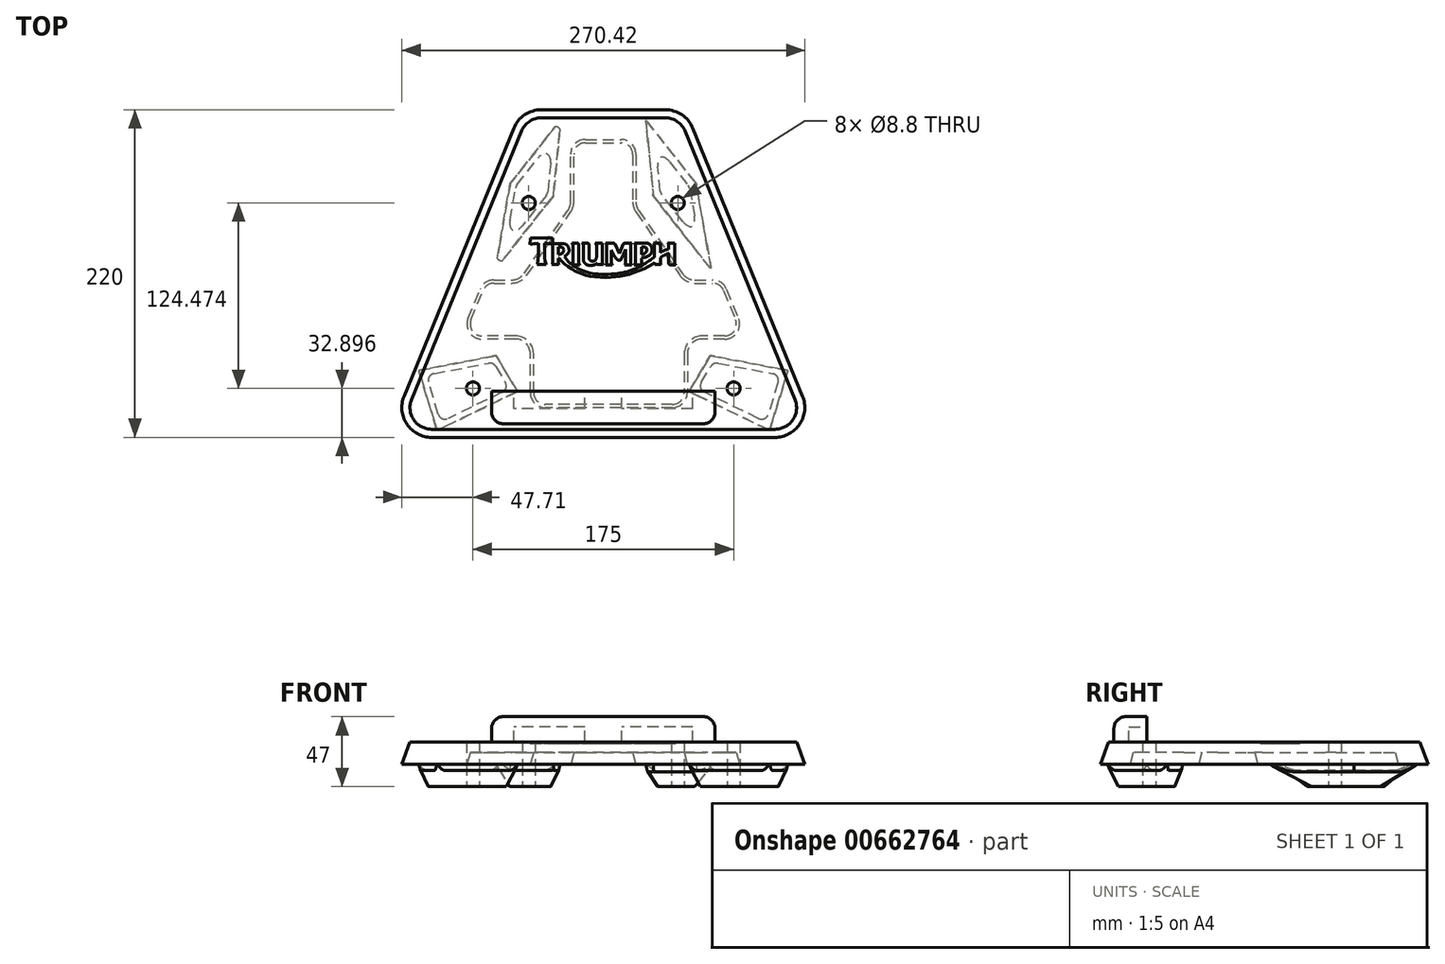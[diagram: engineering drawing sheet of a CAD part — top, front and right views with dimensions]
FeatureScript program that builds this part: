
annotation { "Feature Type Name" : "Feature", "Feature Type Description" : "" }
export const myFeature = defineFeature(function(context is Context, id is Id, definition is map)
    precondition{}
    {
        {
            var Q0;
            Q0=qCreatedBy(makeId("Top.planeOp"),FACE);
            var sketch = newSketch(context, id + "F0", { "sketchPlane" : qUnion([Q0])});
            skPoint(sketch, "E0", {"position": v(-87.5, -62.1) * mm});
            skPoint(sketch, "E1", {"position": v(87.5, -62.1) * mm});
            skPoint(sketch, "E2", {"position": v(50, 62.37) * mm});
            skPoint(sketch, "E3", {"position": v(-50, 62.37) * mm});
            skCircle(sketch, "E4", {"center": v(-50, 62.37) * mm, "radius": 4 * mm});
            skCircle(sketch, "E5", {"center": v(50, 62.37) * mm, "radius": 4 * mm});
            skCircle(sketch, "E6", {"center": v(87.5, -62.1) * mm, "radius": 4 * mm});
            skCircle(sketch, "E7", {"center": v(-87.5, -62.1) * mm, "radius": 4 * mm});
            skSolve(sketch);
        }
        {
            var Q0;
            Q0=qCreatedBy(makeId("Top.planeOp"),FACE);
            var sketch = newSketch(context, id + "F1", { "sketchPlane" : qUnion([Q0])});
            skLineSegment(sketch, "E8.0", {"start": v(72.5, 17.72) * mm, "end": v(62.5, 75.32) * mm});
            skLineSegment(sketch, "E8.1", {"start": v(62.5, 75.32) * mm, "end": v(28.5, 118.39) * mm});
            skLineSegment(sketch, "E8.2", {"start": v(28.5, 118.39) * mm, "end": v(33.5, 67.12) * mm});
            skLineSegment(sketch, "E9", {"start": v(72.5, 17.72) * mm, "end": v(33.5, 67.12) * mm});
            skLineSegment(sketch, "E10", {"start": v(-62.5, 75.32) * mm, "end": v(-28.5, 118.39) * mm});
            skLineSegment(sketch, "E11", {"start": v(-28.5, 118.39) * mm, "end": v(-33.5, 67.12) * mm});
            skLineSegment(sketch, "E12", {"start": v(-33.5, 67.12) * mm, "end": v(-72.5, 17.72) * mm});
            skLineSegment(sketch, "E13", {"start": v(-72.5, 17.72) * mm, "end": v(-62.5, 75.32) * mm});
            skPoint(sketch, "E14", {"position": v(-71.85, -40.1) * mm});
            skPoint(sketch, "E15", {"position": v(-57.57, -64.2) * mm});
            skPoint(sketch, "E16", {"position": v(-123.9, -50.1) * mm});
            skPoint(sketch, "E17", {"position": v(-111.61, -90.27) * mm});
            skPoint(sketch, "E18", {"position": v(71.85, -40.1) * mm});
            skPoint(sketch, "E19", {"position": v(57.57, -64.2) * mm});
            skPoint(sketch, "E20", {"position": v(123.9, -50.1) * mm});
            skPoint(sketch, "E21", {"position": v(111.61, -90.27) * mm});
            skLineSegment(sketch, "E22", {"start": v(-123.9, -50.1) * mm, "end": v(-71.85, -40.1) * mm});
            skLineSegment(sketch, "E23", {"start": v(-57.57, -64.2) * mm, "end": v(-71.85, -40.1) * mm});
            skLineSegment(sketch, "E24", {"start": v(-57.57, -64.2) * mm, "end": v(-111.61, -90.27) * mm});
            skLineSegment(sketch, "E25", {"start": v(-111.61, -90.27) * mm, "end": v(-123.9, -50.1) * mm});
            skLineSegment(sketch, "E26", {"start": v(57.57, -64.2) * mm, "end": v(71.85, -40.1) * mm});
            skLineSegment(sketch, "E27", {"start": v(71.85, -40.1) * mm, "end": v(123.9, -50.1) * mm});
            skLineSegment(sketch, "E28", {"start": v(123.9, -50.1) * mm, "end": v(111.61, -90.27) * mm});
            skLineSegment(sketch, "E29", {"start": v(111.61, -90.27) * mm, "end": v(57.57, -64.2) * mm});
            skSolve(sketch);
        }
        {
            var Q0;
            Q0=makeQuery(id+"F1.imprint","IMPRINT",FACE,{"disambiguationData":[TD([[makeQuery(id+"F1.imprint","IMPRINT",EDGE,{"derivedFrom":sQuery(id+"F1.wireOp",EDGE,"E22")}),-1.0]])]});
            var Q1;
            Q1=makeQuery(id+"F1.imprint","IMPRINT",FACE,{"disambiguationData":[TD([[makeQuery(id+"F1.imprint","IMPRINT",EDGE,{"derivedFrom":sQuery(id+"F1.wireOp",EDGE,"E10")}),-1.0]])]});
            var Q2;
            Q2=makeQuery(id+"F1.imprint","IMPRINT",FACE,{"disambiguationData":[TD([[makeQuery(id+"F1.imprint","IMPRINT",EDGE,{"derivedFrom":sQuery(id+"F1.wireOp",EDGE,"E8.0")}),1.0]])]});
            var Q3;
            Q3=makeQuery(id+"F1.imprint","IMPRINT",FACE,{"disambiguationData":[TD([[makeQuery(id+"F1.imprint","IMPRINT",EDGE,{"derivedFrom":sQuery(id+"F1.wireOp",EDGE,"E26")}),-1.0]])]});
            extrude(context, id + "F2", {"entities" : qUnion([Q0, Q1, Q2, Q3]), "depth" : 15 * mm, "offsetDistance" : 25 * mm});
        }
        {
            var Q0;
            Q0=makeQuery(id+"F2.opExtrude","CAP_FACE",FACE,{"disambiguationData":[OSD([sQuery(id+"F1.wireOp",EDGE,"E10"),sQuery(id+"F1.wireOp",EDGE,"E11"),sQuery(id+"F1.wireOp",EDGE,"E12"),sQuery(id+"F1.wireOp",EDGE,"E13")])],"isStart":false});
            var sketch = newSketch(context, id + "F3", { "sketchPlane" : qUnion([Q0])});
            skLineSegment(sketch, "E30.bottom", {"start": v(-41.57, 125) * mm, "end": v(41.57, 125) * mm});
            skLineSegment(sketch, "E30.top", {"start": v(-115.2, -95) * mm, "end": v(115.2, -95) * mm});
            skLineSegment(sketch, "E30.left", {"start": v(-60.08, 112.57) * mm, "end": v(-133.72, -67.43) * mm});
            skLineSegment(sketch, "E30.right", {"start": v(60.08, 112.57) * mm, "end": v(133.72, -67.43) * mm});
            skPoint(sketch, "E31.visualSharp", {"position": v(-145, -95) * mm});
            skArc(sketch, "E31.filletArc", {"start": v(-133.72, -67.43) * mm, "mid": v(-131.81, -86.15) * mm, "end": v(-115.2, -95) * mm});
            skPoint(sketch, "E32.visualSharp", {"position": v(145, -95) * mm});
            skArc(sketch, "E32.filletArc", {"start": v(115.2, -95) * mm, "mid": v(131.81, -86.15) * mm, "end": v(133.72, -67.43) * mm});
            skPoint(sketch, "E33.visualSharp", {"position": v(55, 125) * mm});
            skArc(sketch, "E33.filletArc", {"start": v(60.08, 112.57) * mm, "mid": v(52.72, 121.6) * mm, "end": v(41.57, 125) * mm});
            skPoint(sketch, "E34.visualSharp", {"position": v(-55, 125) * mm});
            skArc(sketch, "E34.filletArc", {"start": v(-41.57, 125) * mm, "mid": v(-52.72, 121.6) * mm, "end": v(-60.08, 112.57) * mm});
            skSolve(sketch);
        }
        {
            var Q0;
            Q0=makeQuery(id+"F3.imprint","IMPRINT",FACE,{"disambiguationData":[TD([[makeQuery(id+"F3.imprint","IMPRINT",EDGE,{"derivedFrom":sQuery(id+"F3.wireOp",EDGE,"E30.bottom")}),-1.0]])]});
            var Q1;
            Q1=makeQuery(id+"F3.imprint","IMPRINT",FACE,{"disambiguationData":[TD([[makeQuery(id+"F3.imprint","IMPRINT",EDGE,{"derivedFrom":makeQuery(id+"F2.opExtrude","CAP_EDGE",EDGE,{"disambiguationData":[OSD([sQuery(id+"F1.wireOp",EDGE,"E10")])],"isStart":false})}),-1.0]])]});
            extrude(context, id + "F4", {"entities" : qUnion([Q0, Q1]), "depth" : 15 * mm, "offsetDistance" : 25 * mm});
        }
        {
            var Q0;
            Q0=makeQuery(id+"F4.opExtrude","CAP_FACE",FACE,{"disambiguationData":[OSD([sQuery(id+"F3.wireOp",EDGE,"E30.bottom"),sQuery(id+"F3.wireOp",EDGE,"E30.top"),sQuery(id+"F3.wireOp",EDGE,"E30.left"),sQuery(id+"F3.wireOp",EDGE,"E30.right"),sQuery(id+"F3.wireOp",EDGE,"E31.filletArc"),sQuery(id+"F3.wireOp",EDGE,"E32.filletArc"),sQuery(id+"F3.wireOp",EDGE,"E33.filletArc"),sQuery(id+"F3.wireOp",EDGE,"E34.filletArc")])],"isStart":false});
            chamfer(context, id + "F5", {"entities" : qUnion([Q0]), "chamferType" : ChamferType.OFFSET_ANGLE, "width" : 15 * mm, "oppositeDirection" : false, "angle" : 20 * degree, "tangentPropagation" : true});
        }
        {
            var Q0;
            Q0=sQuery(id+"F0.wireOp",VERTEX,"E7.center");
            var Q1;
            Q1=sQuery(id+"F0.wireOp",VERTEX,"E4.center");
            var Q2;
            Q2=sQuery(id+"F0.wireOp",VERTEX,"E2");
            var Q3;
            Q3=sQuery(id+"F0.wireOp",VERTEX,"E1");
            var Q4;
            Q4=makeQuery(id+"F2.opExtrude","SWEPT_BODY",BODY,{"disambiguationData":[OSD([sQuery(id+"F1.wireOp",EDGE,"E22"),sQuery(id+"F1.wireOp",EDGE,"E23"),sQuery(id+"F1.wireOp",EDGE,"E24"),sQuery(id+"F1.wireOp",EDGE,"E25")])]});
            var Q5;
            Q5=makeQuery(id+"F4.opExtrude","SWEPT_BODY",BODY,{"disambiguationData":[OSD([sQuery(id+"F3.wireOp",EDGE,"E30.bottom"),sQuery(id+"F3.wireOp",EDGE,"E30.top"),sQuery(id+"F3.wireOp",EDGE,"E30.left"),sQuery(id+"F3.wireOp",EDGE,"E30.right"),sQuery(id+"F3.wireOp",EDGE,"E31.filletArc"),sQuery(id+"F3.wireOp",EDGE,"E32.filletArc"),sQuery(id+"F3.wireOp",EDGE,"E33.filletArc"),sQuery(id+"F3.wireOp",EDGE,"E34.filletArc")])]});
            var Q6;
            Q6=makeQuery(id+"F2.opExtrude","SWEPT_BODY",BODY,{"disambiguationData":[OSD([sQuery(id+"F1.wireOp",EDGE,"E10"),sQuery(id+"F1.wireOp",EDGE,"E11"),sQuery(id+"F1.wireOp",EDGE,"E12"),sQuery(id+"F1.wireOp",EDGE,"E13")])]});
            var Q7;
            Q7=makeQuery(id+"F2.opExtrude","SWEPT_BODY",BODY,{"disambiguationData":[OSD([sQuery(id+"F1.wireOp",EDGE,"E8.0"),sQuery(id+"F1.wireOp",EDGE,"E8.1"),sQuery(id+"F1.wireOp",EDGE,"E8.2"),sQuery(id+"F1.wireOp",EDGE,"E9")])]});
            var Q8;
            Q8=makeQuery(id+"F2.opExtrude","SWEPT_BODY",BODY,{"disambiguationData":[OSD([sQuery(id+"F1.wireOp",EDGE,"E26"),sQuery(id+"F1.wireOp",EDGE,"E27"),sQuery(id+"F1.wireOp",EDGE,"E28"),sQuery(id+"F1.wireOp",EDGE,"E29")])]});
            hole(context, id + "F6", {"style" : HoleStyle.SIMPLE, "endStyle" : HoleEndStyle.THROUGH, "oppositeDirection" : true, "standardTappedOrClearance" : lookupTablePath({ "standard" : "ISO", "fit" : "Normal", "size" : "M8", "type" : "Clearance" }), "standardBlindInLast" : lookupTablePath({ "fit" : "Standard", "standard" : "ISO", "size" : "M8", "type" : "Clearance" }), "holeDiameter" : 8.8 * mm, "majorDiameter" : 5 * mm, "isTappedThrough" : true, "tappedDepth" : 12 * mm, "tapClearance" : 3, "locations" : qUnion([Q0, Q1, Q2, Q3]), "scope" : qUnion([Q4, Q5, Q6, Q7, Q8])});
        }
        {
            var Q0;
            Q0=makeQuery(id+"F4.opExtrude","CAP_FACE",FACE,{"disambiguationData":[OSD([sQuery(id+"F3.wireOp",EDGE,"E30.bottom"),sQuery(id+"F3.wireOp",EDGE,"E30.top"),sQuery(id+"F3.wireOp",EDGE,"E30.left"),sQuery(id+"F3.wireOp",EDGE,"E30.right"),sQuery(id+"F3.wireOp",EDGE,"E31.filletArc"),sQuery(id+"F3.wireOp",EDGE,"E32.filletArc"),sQuery(id+"F3.wireOp",EDGE,"E33.filletArc"),sQuery(id+"F3.wireOp",EDGE,"E34.filletArc")])],"isStart":true});
            var sketch = newSketch(context, id + "F7", { "sketchPlane" : qUnion([Q0])});
            skLineSegment(sketch, "E35.0", {"start": v(-115.2, 75) * mm, "end": v(-115.2, 75) * mm});
            skLineSegment(sketch, "E35.1", {"start": v(-82.69, -4.5) * mm, "end": v(-90.76, 15.23) * mm});
            skLineSegment(sketch, "E35.2", {"start": v(-38.95, 75) * mm, "end": v(46.4, 75) * mm});
            skLineSegment(sketch, "E35.3", {"start": v(-41.57, -105) * mm, "end": v(-41.57, -105) * mm});
            skLineSegment(sketch, "E35.4", {"start": v(115.2, 75) * mm, "end": v(115.2, 75) * mm});
            skLineSegment(sketch, "E35.5", {"start": v(82.69, -4.5) * mm, "end": v(90.76, 15.23) * mm});
            skLineSegment(sketch, "E35.6", {"start": v(41.57, -105) * mm, "end": v(41.57, -105) * mm});
            skLineSegment(sketch, "E35.7", {"start": v(-11.93, -105) * mm, "end": v(11.93, -105) * mm});
            skLineSegment(sketch, "E36", {"start": v(-81.5, 29.02) * mm, "end": v(-58.95, 29.02) * mm});
            skLineSegment(sketch, "E37", {"start": v(-48.95, 65) * mm, "end": v(-48.95, 39.02) * mm});
            skLineSegment(sketch, "E38", {"start": v(81.5, 29.02) * mm, "end": v(66.4, 29.02) * mm});
            skLineSegment(sketch, "E39", {"start": v(56.4, 65) * mm, "end": v(56.4, 39.02) * mm});
            skPoint(sketch, "E40.newPointA", {"position": v(-88.95, 29.02) * mm});
            skArc(sketch, "E40.filletArc", {"start": v(-81.5, 29.02) * mm, "mid": v(-89.8, 24.59) * mm, "end": v(-90.76, 15.23) * mm});
            skPoint(sketch, "E41.visualSharp", {"position": v(-48.95, 29.02) * mm});
            skArc(sketch, "E41.filletArc", {"start": v(-58.95, 29.02) * mm, "mid": v(-51.88, 31.94) * mm, "end": v(-48.95, 39.02) * mm});
            skPoint(sketch, "E42.newPointA", {"position": v(-48.95, 75) * mm});
            skArc(sketch, "E42.filletArc", {"start": v(-38.95, 75) * mm, "mid": v(-46.02, 72.07) * mm, "end": v(-48.95, 65) * mm});
            skPoint(sketch, "E43.newPointB", {"position": v(56.4, 75) * mm});
            skArc(sketch, "E43.filletArc", {"start": v(56.4, 65) * mm, "mid": v(53.47, 72.07) * mm, "end": v(46.4, 75) * mm});
            skPoint(sketch, "E44.visualSharp", {"position": v(56.4, 29.02) * mm});
            skArc(sketch, "E44.filletArc", {"start": v(56.4, 39.02) * mm, "mid": v(59.33, 31.94) * mm, "end": v(66.4, 29.02) * mm});
            skPoint(sketch, "E45.newPointA", {"position": v(96.4, 29.02) * mm});
            skArc(sketch, "E45.filletArc", {"start": v(90.76, 15.23) * mm, "mid": v(89.8, 24.59) * mm, "end": v(81.5, 29.02) * mm});
            skLineSegment(sketch, "E46", {"start": v(-73.43, -10.71) * mm, "end": v(-61.38, -10.71) * mm});
            skLineSegment(sketch, "E47", {"start": v(73.43, -10.71) * mm, "end": v(61.38, -10.71) * mm});
            skLineSegment(sketch, "E48", {"start": v(-21.93, -95) * mm, "end": v(-21.93, -63.13) * mm});
            skLineSegment(sketch, "E49", {"start": v(-23.71, -57.43) * mm, "end": v(-53.16, -15) * mm});
            skLineSegment(sketch, "E50", {"start": v(21.93, -95) * mm, "end": v(21.93, -63.13) * mm});
            skLineSegment(sketch, "E51", {"start": v(23.71, -57.43) * mm, "end": v(53.16, -15) * mm});
            skPoint(sketch, "E52.newPointA", {"position": v(-80.15, -10.71) * mm});
            skArc(sketch, "E52.filletArc", {"start": v(-82.69, -4.5) * mm, "mid": v(-79, -9.01) * mm, "end": v(-73.43, -10.71) * mm});
            skPoint(sketch, "E53.visualSharp", {"position": v(-56.15, -10.71) * mm});
            skArc(sketch, "E53.filletArc", {"start": v(-53.16, -15) * mm, "mid": v(-56.74, -11.85) * mm, "end": v(-61.38, -10.71) * mm});
            skPoint(sketch, "E54.visualSharp", {"position": v(-21.93, -60) * mm});
            skArc(sketch, "E54.filletArc", {"start": v(-21.93, -63.13) * mm, "mid": v(-22.38, -60.14) * mm, "end": v(-23.71, -57.43) * mm});
            skPoint(sketch, "E55.newPointA", {"position": v(-21.93, -105) * mm});
            skArc(sketch, "E55.filletArc", {"start": v(-21.93, -95) * mm, "mid": v(-19, -102.07) * mm, "end": v(-11.93, -105) * mm});
            skPoint(sketch, "E56.newPointA", {"position": v(21.93, -105) * mm});
            skArc(sketch, "E56.filletArc", {"start": v(11.93, -105) * mm, "mid": v(19, -102.07) * mm, "end": v(21.93, -95) * mm});
            skPoint(sketch, "E57.visualSharp", {"position": v(21.93, -60) * mm});
            skArc(sketch, "E57.filletArc", {"start": v(23.71, -57.43) * mm, "mid": v(22.38, -60.14) * mm, "end": v(21.93, -63.13) * mm});
            skPoint(sketch, "E58.visualSharp", {"position": v(56.15, -10.71) * mm});
            skArc(sketch, "E58.filletArc", {"start": v(61.38, -10.71) * mm, "mid": v(56.74, -11.85) * mm, "end": v(53.16, -15) * mm});
            skPoint(sketch, "E59.newPointA", {"position": v(80.15, -10.71) * mm});
            skArc(sketch, "E59.filletArc", {"start": v(73.43, -10.71) * mm, "mid": v(79, -9.01) * mm, "end": v(82.69, -4.5) * mm});
            skSolve(sketch);
        }
        {
            var Q0;
            Q0=makeQuery(id+"F7.imprint","IMPRINT",FACE,{"disambiguationData":[TD([[makeQuery(id+"F7.imprint","IMPRINT",EDGE,{"derivedFrom":sQuery(id+"F7.wireOp",EDGE,"E35.1")}),-1.0]])]});
            extrude(context, id + "F8", {"entities" : qUnion([Q0]), "operationType" : NewBodyOperationType.REMOVE, "oppositeDirection" : true, "depth" : 8 * mm, "offsetDistance" : 25 * mm, "hasDraft" : true, "draftAngle" : 15 * degree, "draftPullDirection" : true});
        }
        {
            var Q0;
            Q0=makeQuery(id+"F2.opExtrude","CAP_EDGE",EDGE,{"disambiguationData":[OSD([sQuery(id+"F1.wireOp",EDGE,"E27")])],"isStart":true});
            var Q1;
            Q1=makeQuery(id+"F2.opExtrude","CAP_EDGE",EDGE,{"disambiguationData":[OSD([sQuery(id+"F1.wireOp",EDGE,"E28")])],"isStart":true});
            var Q2;
            Q2=makeQuery(id+"F2.opExtrude","CAP_EDGE",EDGE,{"disambiguationData":[OSD([sQuery(id+"F1.wireOp",EDGE,"E29")])],"isStart":true});
            var Q3;
            Q3=makeQuery(id+"F2.opExtrude","CAP_EDGE",EDGE,{"disambiguationData":[OSD([sQuery(id+"F1.wireOp",EDGE,"E26")])],"isStart":true});
            var Q4;
            Q4=makeQuery(id+"F2.opExtrude","CAP_EDGE",EDGE,{"disambiguationData":[OSD([sQuery(id+"F1.wireOp",EDGE,"E25")])],"isStart":true});
            var Q5;
            Q5=makeQuery(id+"F2.opExtrude","CAP_EDGE",EDGE,{"disambiguationData":[OSD([sQuery(id+"F1.wireOp",EDGE,"E24")])],"isStart":true});
            var Q6;
            Q6=makeQuery(id+"F2.opExtrude","CAP_EDGE",EDGE,{"disambiguationData":[OSD([sQuery(id+"F1.wireOp",EDGE,"E23")])],"isStart":true});
            var Q7;
            Q7=makeQuery(id+"F2.opExtrude","CAP_EDGE",EDGE,{"disambiguationData":[OSD([sQuery(id+"F1.wireOp",EDGE,"E22")])],"isStart":true});
            var Q8;
            Q8=makeQuery(id+"F2.opExtrude","CAP_EDGE",EDGE,{"disambiguationData":[OSD([sQuery(id+"F1.wireOp",EDGE,"E11")])],"isStart":true});
            var Q9;
            Q9=makeQuery(id+"F2.opExtrude","CAP_EDGE",EDGE,{"disambiguationData":[OSD([sQuery(id+"F1.wireOp",EDGE,"E10")])],"isStart":true});
            var Q10;
            Q10=makeQuery(id+"F2.opExtrude","CAP_EDGE",EDGE,{"disambiguationData":[OSD([sQuery(id+"F1.wireOp",EDGE,"E13")])],"isStart":true});
            var Q11;
            Q11=makeQuery(id+"F2.opExtrude","CAP_EDGE",EDGE,{"disambiguationData":[OSD([sQuery(id+"F1.wireOp",EDGE,"E12")])],"isStart":true});
            chamfer(context, id + "F9", {"entities" : qUnion([Q0, Q1, Q2, Q3, Q4, Q5, Q6, Q7, Q8, Q9, Q10, Q11]), "chamferType" : ChamferType.TWO_OFFSETS, "width1" : 4 * mm, "oppositeDirection" : false, "width2" : 11 * mm, "tangentPropagation" : true});
        }
        {
            var Q0;
            Q0=makeQuery(id+"F2.opExtrude","CAP_EDGE",EDGE,{"disambiguationData":[OSD([sQuery(id+"F1.wireOp",EDGE,"E8.1")])],"isStart":true});
            var Q1;
            Q1=makeQuery(id+"F2.opExtrude","CAP_EDGE",EDGE,{"disambiguationData":[OSD([sQuery(id+"F1.wireOp",EDGE,"E8.2")])],"isStart":true});
            var Q2;
            Q2=makeQuery(id+"F2.opExtrude","CAP_EDGE",EDGE,{"disambiguationData":[OSD([sQuery(id+"F1.wireOp",EDGE,"E9")])],"isStart":true});
            var Q3;
            Q3=makeQuery(id+"F2.opExtrude","CAP_EDGE",EDGE,{"disambiguationData":[OSD([sQuery(id+"F1.wireOp",EDGE,"E8.0")])],"isStart":true});
            chamfer(context, id + "F10", {"entities" : qUnion([Q0, Q1, Q2, Q3]), "chamferType" : ChamferType.TWO_OFFSETS, "width1" : 10 * mm, "oppositeDirection" : false, "width2" : 5 * mm, "tangentPropagation" : true});
        }
        {
            var Q0;
            Q0=makeQuery(id+"F9.opChamfer","BLEND_EDGE",EDGE,{"blendedFrom":[makeQuery(id+"F2.opExtrude","CAP_EDGE",EDGE,{"disambiguationData":[OSD([sQuery(id+"F1.wireOp",EDGE,"E24")])],"isStart":true}),makeQuery(id+"F2.opExtrude","CAP_EDGE",EDGE,{"disambiguationData":[OSD([sQuery(id+"F1.wireOp",EDGE,"E25")])],"isStart":true})],"blendedInto":[]});
            var Q1;
            Q1=makeQuery(id+"F9.opChamfer","BLEND_EDGE",EDGE,{"blendedFrom":[makeQuery(id+"F2.opExtrude","CAP_EDGE",EDGE,{"disambiguationData":[OSD([sQuery(id+"F1.wireOp",EDGE,"E22")])],"isStart":true}),makeQuery(id+"F2.opExtrude","CAP_EDGE",EDGE,{"disambiguationData":[OSD([sQuery(id+"F1.wireOp",EDGE,"E25")])],"isStart":true})],"blendedInto":[]});
            var Q2;
            Q2=makeQuery(id+"F9.opChamfer","BLEND_EDGE",EDGE,{"blendedFrom":[makeQuery(id+"F2.opExtrude","CAP_EDGE",EDGE,{"disambiguationData":[OSD([sQuery(id+"F1.wireOp",EDGE,"E22")])],"isStart":true}),makeQuery(id+"F2.opExtrude","CAP_EDGE",EDGE,{"disambiguationData":[OSD([sQuery(id+"F1.wireOp",EDGE,"E23")])],"isStart":true})],"blendedInto":[]});
            var Q3;
            Q3=makeQuery(id+"F9.opChamfer","BLEND_EDGE",EDGE,{"blendedFrom":[makeQuery(id+"F2.opExtrude","CAP_EDGE",EDGE,{"disambiguationData":[OSD([sQuery(id+"F1.wireOp",EDGE,"E23")])],"isStart":true}),makeQuery(id+"F2.opExtrude","CAP_EDGE",EDGE,{"disambiguationData":[OSD([sQuery(id+"F1.wireOp",EDGE,"E24")])],"isStart":true})],"blendedInto":[]});
            var Q4;
            Q4=makeQuery(id+"F9.opChamfer","BLEND_EDGE",EDGE,{"blendedFrom":[makeQuery(id+"F2.opExtrude","CAP_EDGE",EDGE,{"disambiguationData":[OSD([sQuery(id+"F1.wireOp",EDGE,"E26")])],"isStart":true}),makeQuery(id+"F2.opExtrude","CAP_EDGE",EDGE,{"disambiguationData":[OSD([sQuery(id+"F1.wireOp",EDGE,"E29")])],"isStart":true})],"blendedInto":[]});
            var Q5;
            Q5=makeQuery(id+"F9.opChamfer","BLEND_EDGE",EDGE,{"blendedFrom":[makeQuery(id+"F2.opExtrude","CAP_EDGE",EDGE,{"disambiguationData":[OSD([sQuery(id+"F1.wireOp",EDGE,"E28")])],"isStart":true}),makeQuery(id+"F2.opExtrude","CAP_EDGE",EDGE,{"disambiguationData":[OSD([sQuery(id+"F1.wireOp",EDGE,"E29")])],"isStart":true})],"blendedInto":[]});
            var Q6;
            Q6=makeQuery(id+"F9.opChamfer","BLEND_EDGE",EDGE,{"blendedFrom":[makeQuery(id+"F2.opExtrude","CAP_EDGE",EDGE,{"disambiguationData":[OSD([sQuery(id+"F1.wireOp",EDGE,"E27")])],"isStart":true}),makeQuery(id+"F2.opExtrude","CAP_EDGE",EDGE,{"disambiguationData":[OSD([sQuery(id+"F1.wireOp",EDGE,"E28")])],"isStart":true})],"blendedInto":[]});
            var Q7;
            Q7=makeQuery(id+"F9.opChamfer","BLEND_EDGE",EDGE,{"blendedFrom":[makeQuery(id+"F2.opExtrude","CAP_EDGE",EDGE,{"disambiguationData":[OSD([sQuery(id+"F1.wireOp",EDGE,"E26")])],"isStart":true}),makeQuery(id+"F2.opExtrude","CAP_EDGE",EDGE,{"disambiguationData":[OSD([sQuery(id+"F1.wireOp",EDGE,"E27")])],"isStart":true})],"blendedInto":[]});
            var Q8;
            Q8=makeQuery(id+"F10.opChamfer","BLEND_EDGE",EDGE,{"blendedFrom":[makeQuery(id+"F2.opExtrude","CAP_EDGE",EDGE,{"disambiguationData":[OSD([sQuery(id+"F1.wireOp",EDGE,"E8.1")])],"isStart":true}),makeQuery(id+"F2.opExtrude","CAP_EDGE",EDGE,{"disambiguationData":[OSD([sQuery(id+"F1.wireOp",EDGE,"E8.2")])],"isStart":true})],"blendedInto":[]});
            var Q9;
            Q9=makeQuery(id+"F10.opChamfer","BLEND_EDGE",EDGE,{"blendedFrom":[makeQuery(id+"F2.opExtrude","CAP_EDGE",EDGE,{"disambiguationData":[OSD([sQuery(id+"F1.wireOp",EDGE,"E8.2")])],"isStart":true}),makeQuery(id+"F2.opExtrude","CAP_EDGE",EDGE,{"disambiguationData":[OSD([sQuery(id+"F1.wireOp",EDGE,"E9")])],"isStart":true})],"blendedInto":[]});
            var Q10;
            Q10=makeQuery(id+"F10.opChamfer","BLEND_EDGE",EDGE,{"blendedFrom":[makeQuery(id+"F2.opExtrude","CAP_EDGE",EDGE,{"disambiguationData":[OSD([sQuery(id+"F1.wireOp",EDGE,"E8.0")])],"isStart":true}),makeQuery(id+"F2.opExtrude","CAP_EDGE",EDGE,{"disambiguationData":[OSD([sQuery(id+"F1.wireOp",EDGE,"E9")])],"isStart":true})],"blendedInto":[]});
            var Q11;
            Q11=makeQuery(id+"F10.opChamfer","BLEND_EDGE",EDGE,{"blendedFrom":[makeQuery(id+"F2.opExtrude","CAP_EDGE",EDGE,{"disambiguationData":[OSD([sQuery(id+"F1.wireOp",EDGE,"E8.0")])],"isStart":true}),makeQuery(id+"F2.opExtrude","CAP_EDGE",EDGE,{"disambiguationData":[OSD([sQuery(id+"F1.wireOp",EDGE,"E8.1")])],"isStart":true})],"blendedInto":[]});
            var Q12;
            Q12=makeQuery(id+"F9.opChamfer","BLEND_EDGE",EDGE,{"blendedFrom":[makeQuery(id+"F2.opExtrude","CAP_EDGE",EDGE,{"disambiguationData":[OSD([sQuery(id+"F1.wireOp",EDGE,"E11")])],"isStart":true}),makeQuery(id+"F2.opExtrude","CAP_EDGE",EDGE,{"disambiguationData":[OSD([sQuery(id+"F1.wireOp",EDGE,"E12")])],"isStart":true})],"blendedInto":[]});
            var Q13;
            Q13=makeQuery(id+"F9.opChamfer","BLEND_EDGE",EDGE,{"blendedFrom":[makeQuery(id+"F2.opExtrude","CAP_EDGE",EDGE,{"disambiguationData":[OSD([sQuery(id+"F1.wireOp",EDGE,"E10")])],"isStart":true}),makeQuery(id+"F2.opExtrude","CAP_EDGE",EDGE,{"disambiguationData":[OSD([sQuery(id+"F1.wireOp",EDGE,"E11")])],"isStart":true})],"blendedInto":[]});
            var Q14;
            Q14=makeQuery(id+"F9.opChamfer","BLEND_EDGE",EDGE,{"blendedFrom":[makeQuery(id+"F2.opExtrude","CAP_EDGE",EDGE,{"disambiguationData":[OSD([sQuery(id+"F1.wireOp",EDGE,"E10")])],"isStart":true}),makeQuery(id+"F2.opExtrude","CAP_EDGE",EDGE,{"disambiguationData":[OSD([sQuery(id+"F1.wireOp",EDGE,"E13")])],"isStart":true})],"blendedInto":[]});
            var Q15;
            Q15=makeQuery(id+"F9.opChamfer","BLEND_EDGE",EDGE,{"blendedFrom":[makeQuery(id+"F2.opExtrude","CAP_EDGE",EDGE,{"disambiguationData":[OSD([sQuery(id+"F1.wireOp",EDGE,"E12")])],"isStart":true}),makeQuery(id+"F2.opExtrude","CAP_EDGE",EDGE,{"disambiguationData":[OSD([sQuery(id+"F1.wireOp",EDGE,"E13")])],"isStart":true})],"blendedInto":[]});
            fillet(context, id + "F11", {"entities" : qUnion([Q0, Q1, Q2, Q3, Q4, Q5, Q6, Q7, Q8, Q9, Q10, Q11, Q12, Q13, Q14, Q15]), "radius" : 5 * mm, "tangentPropagation" : true, "allowEdgeOverflow" : false});
        }
        {
            var Q0;
            Q0=makeQuery(id+"F4.opExtrude","CAP_FACE",FACE,{"disambiguationData":[OSD([sQuery(id+"F3.wireOp",EDGE,"E30.bottom"),sQuery(id+"F3.wireOp",EDGE,"E30.top"),sQuery(id+"F3.wireOp",EDGE,"E30.left"),sQuery(id+"F3.wireOp",EDGE,"E30.right"),sQuery(id+"F3.wireOp",EDGE,"E31.filletArc"),sQuery(id+"F3.wireOp",EDGE,"E32.filletArc"),sQuery(id+"F3.wireOp",EDGE,"E33.filletArc"),sQuery(id+"F3.wireOp",EDGE,"E34.filletArc")])],"isStart":false});
            var sketch = newSketch(context, id + "F12", { "sketchPlane" : qUnion([Q0])});
            skLineSegment(sketch, "E60", {"start": v(-48.95, 39) * mm, "end": v(-33.85, 39) * mm});
            skLineSegment(sketch, "E61", {"start": v(-33.85, 39) * mm, "end": v(-33.85, 33.8) * mm});
            skLineSegment(sketch, "E62", {"start": v(-33.85, 33.8) * mm, "end": v(-34.12, 34.22) * mm});
            skLineSegment(sketch, "E63", {"start": v(-34.12, 34.22) * mm, "end": v(-34.68, 34.65) * mm});
            skLineSegment(sketch, "E64", {"start": v(-34.68, 34.65) * mm, "end": v(-35.58, 34.95) * mm});
            skLineSegment(sketch, "E65", {"start": v(-35.58, 34.95) * mm, "end": v(-37.14, 35.23) * mm});
            skLineSegment(sketch, "E66", {"start": v(-37.14, 35.23) * mm, "end": v(-38.22, 35.25) * mm});
            skLineSegment(sketch, "E67", {"start": v(-38.22, 35.25) * mm, "end": v(-39.33, 35.28) * mm});
            skLineSegment(sketch, "E68", {"start": v(-39.33, 35.28) * mm, "end": v(-39.3, 28.6) * mm});
            skLineSegment(sketch, "E69", {"start": v(-39.3, 28.6) * mm, "end": v(-39.2, 25.68) * mm});
            skLineSegment(sketch, "E70", {"start": v(-39.2, 25.68) * mm, "end": v(-38.95, 23.34) * mm});
            skLineSegment(sketch, "E71", {"start": v(-38.95, 23.34) * mm, "end": v(-38.45, 21.43) * mm});
            skLineSegment(sketch, "E72", {"start": v(-38.45, 21.43) * mm, "end": v(-38.27, 21) * mm});
            skLineSegment(sketch, "E73", {"start": v(-38.27, 21) * mm, "end": v(-44.43, 21) * mm});
            skLineSegment(sketch, "E74", {"start": v(-44.43, 21) * mm, "end": v(-44.2, 21.4) * mm});
            skLineSegment(sketch, "E75", {"start": v(-44.2, 21.4) * mm, "end": v(-43.75, 24.2) * mm});
            skLineSegment(sketch, "E76", {"start": v(-43.75, 24.2) * mm, "end": v(-43.55, 28.6) * mm});
            skLineSegment(sketch, "E77", {"start": v(-43.55, 28.6) * mm, "end": v(-43.55, 35.3) * mm});
            skLineSegment(sketch, "E78", {"start": v(-43.55, 35.3) * mm, "end": v(-45.03, 35.2) * mm});
            skLineSegment(sketch, "E79", {"start": v(-45.03, 35.2) * mm, "end": v(-46.42, 35.1) * mm});
            skLineSegment(sketch, "E80", {"start": v(-46.42, 35.1) * mm, "end": v(-47.85, 34.9) * mm});
            skLineSegment(sketch, "E81", {"start": v(-47.85, 34.9) * mm, "end": v(-48.83, 34.65) * mm});
            skLineSegment(sketch, "E82", {"start": v(-48.83, 34.65) * mm, "end": v(-49.26, 34.47) * mm});
            skLineSegment(sketch, "E83", {"start": v(-49.26, 34.47) * mm, "end": v(-48.95, 39) * mm});
            skLineSegment(sketch, "E84", {"start": v(-34.52, 21.03) * mm, "end": v(-34.1, 21.75) * mm});
            skLineSegment(sketch, "E85", {"start": v(-34.1, 21.75) * mm, "end": v(-34, 22.19) * mm});
            skLineSegment(sketch, "E86", {"start": v(-34, 22.19) * mm, "end": v(-34, 35.23) * mm});
            skLineSegment(sketch, "E87", {"start": v(-34, 35.23) * mm, "end": v(-26.79, 35.23) * mm});
            skFitSpline(sketch, "E88", {"points": [v(-25.52, 34.9) * mm, v(-24, 33.8) * mm, v(-23.2, 32.03) * mm, v(-23, 30.02) * mm, v(-23.6, 28.57) * mm, v(-24.8, 27.3) * mm, v(-26.16, 26.47) * mm], "startDerivative": vector(9.92, -5.57) * mm, "endDerivative": vector(-8.88, -4.74) * mm});
            skFitSpline(sketch, "E89", {"points": [v(-26.16, 26.47) * mm, v(-25.38, 25.35) * mm, v(-23.4, 23.1) * mm, v(-21.99, 21.78) * mm, v(-19.94, 20.2) * mm, v(-17.61, 18.72) * mm, v(-15, 17.42) * mm, v(-11.78, 16.16) * mm, v(-7.47, 15.11) * mm, v(-3.6, 14.65) * mm, v(1.53, 14.53) * mm, v(7.46, 14.83) * mm, v(11.57, 15.34) * mm], "startDerivative": vector(12.1, -18.84) * mm, "endDerivative": vector(41.94, 6.04) * mm});
            skFitSpline(sketch, "E90", {"points": [v(11.57, 15.34) * mm, v(16.1, 16.3) * mm, v(19.74, 17.53) * mm, v(24.39, 19.51) * mm, v(27.18, 21.16) * mm, v(31.91, 24.42) * mm], "startDerivative": vector(23.25, 4.37) * mm, "endDerivative": vector(22.66, 15.76) * mm});
            skFitSpline(sketch, "E91", {"points": [v(31.91, 24.42) * mm, v(34.34, 26.17) * mm], "startDerivative": vector(2.45, 1.82) * mm, "endDerivative": vector(2.45, 1.82) * mm});
            skLineSegment(sketch, "E92", {"start": v(34.34, 26.17) * mm, "end": v(34.34, 34.1) * mm});
            skFitSpline(sketch, "E93", {"points": [v(34.34, 34.1) * mm, v(34.2, 34.6) * mm, v(33.98, 35.04) * mm, v(33.75, 35.3) * mm], "startDerivative": vector(-0.3, 1.45) * mm, "endDerivative": vector(-0.81, 0.8) * mm});
            skLineSegment(sketch, "E94", {"start": v(33.75, 35.3) * mm, "end": v(38.36, 35.3) * mm});
            skLineSegment(sketch, "E95", {"start": v(38.36, 35.3) * mm, "end": v(38.36, 29.17) * mm});
            skFitSpline(sketch, "E96", {"points": [v(38.36, 29.17) * mm, v(39.09, 29.59) * mm, v(39.95, 30.04) * mm, v(40.93, 30.48) * mm, v(42, 30.95) * mm, v(43.22, 31.3) * mm, v(43.91, 31.43) * mm], "startDerivative": vector(4.63, 2.74) * mm, "endDerivative": vector(4.55, 0.67) * mm});
            skLineSegment(sketch, "E97", {"start": v(43.91, 31.43) * mm, "end": v(43.91, 33.95) * mm});
            skFitSpline(sketch, "E98", {"points": [v(43.91, 33.95) * mm, v(43.83, 34.44) * mm, v(43.67, 34.86) * mm, v(43.48, 35.13) * mm, v(43.26, 35.35) * mm], "startDerivative": vector(-0.22, 1.74) * mm, "endDerivative": vector(-1.04, 0.93) * mm});
            skLineSegment(sketch, "E99", {"start": v(43.26, 35.35) * mm, "end": v(47.85, 35.35) * mm});
            skLineSegment(sketch, "E100", {"start": v(47.85, 35.35) * mm, "end": v(47.85, 22.28) * mm});
            skFitSpline(sketch, "E101", {"points": [v(47.85, 22.28) * mm, v(47.93, 21.91) * mm, v(48.08, 21.5) * mm, v(48.29, 21.21) * mm, v(48.48, 20.95) * mm], "startDerivative": vector(0.32, -1.42) * mm, "endDerivative": vector(0.82, -1.14) * mm});
            skLineSegment(sketch, "E102", {"start": v(48.48, 20.95) * mm, "end": v(44.63, 20.95) * mm});
            skFitSpline(sketch, "E103", {"points": [v(44.63, 20.95) * mm, v(44.4, 21.07) * mm, v(44.12, 21.33) * mm, v(43.95, 21.75) * mm], "startDerivative": vector(-0.76, 0.39) * mm, "endDerivative": vector(-0.34, 1.22) * mm});
            skLineSegment(sketch, "E104", {"start": v(43.95, 21.75) * mm, "end": v(43.95, 28.67) * mm});
            skFitSpline(sketch, "E105", {"points": [v(43.95, 28.67) * mm, v(42.62, 28.13) * mm, v(41.25, 27.49) * mm, v(40.13, 26.87) * mm, v(39.2, 26.3) * mm, v(38.42, 25.58) * mm], "startDerivative": vector(-6.21, -2.46) * mm, "endDerivative": vector(-4.07, -4.12) * mm});
            skLineSegment(sketch, "E106", {"start": v(38.42, 25.58) * mm, "end": v(38.42, 21.88) * mm});
            skFitSpline(sketch, "E107", {"points": [v(38.42, 21.88) * mm, v(38.47, 21.62) * mm, v(38.6, 21.32) * mm, v(38.72, 21.14) * mm, v(38.83, 21.04) * mm], "startDerivative": vector(0.11, -0.96) * mm, "endDerivative": vector(0.6, -0.47) * mm});
            skLineSegment(sketch, "E108", {"start": v(38.83, 21.04) * mm, "end": v(35.07, 21.04) * mm});
            skFitSpline(sketch, "E109", {"points": [v(35.07, 21.04) * mm, v(34.63, 21.31) * mm, v(34.4, 21.84) * mm, v(34.32, 22.42) * mm], "startDerivative": vector(-1.54, 0.68) * mm, "endDerivative": vector(-0.15, 1.69) * mm});
            skFitSpline(sketch, "E110", {"points": [v(34.32, 22.42) * mm, v(31.58, 20.5) * mm, v(24.62, 17.09) * mm, v(16.2, 14.27) * mm, v(9.24, 12.93) * mm, v(2.2, 12.35) * mm, v(-6.88, 12.93) * mm, v(-12.63, 14.26) * mm, v(-16.9, 15.84) * mm, v(-21.76, 18.38) * mm, v(-26.28, 21.67) * mm, v(-29.68, 25.3) * mm], "startDerivative": vector(-35.8, -27.35) * mm, "endDerivative": vector(-39.38, 45.8) * mm});
            skLineSegment(sketch, "E111", {"start": v(-29.68, 25.3) * mm, "end": v(-30.15, 25.3) * mm});
            skLineSegment(sketch, "E112", {"start": v(-30.15, 25.3) * mm, "end": v(-30.15, 22.02) * mm});
            skFitSpline(sketch, "E113", {"points": [v(-30.15, 22.02) * mm, v(-30.15, 21.62) * mm, v(-29.78, 21) * mm], "startDerivative": vector(-0.14, -0.91) * mm, "endDerivative": vector(0.84, -1.14) * mm});
            skLineSegment(sketch, "E114", {"start": v(-34.52, 21.03) * mm, "end": v(-29.78, 21) * mm});
            skLineSegment(sketch, "E115", {"start": v(-30.3, 27.81) * mm, "end": v(-30.3, 32.82) * mm});
            skLineSegment(sketch, "E116", {"start": v(-30.3, 32.82) * mm, "end": v(-29.29, 32.89) * mm});
            skFitSpline(sketch, "E117", {"points": [v(-29.29, 32.89) * mm, v(-28.23, 32.78) * mm, v(-27.32, 32.38) * mm, v(-26.6, 31.54) * mm, v(-26.56, 30.27) * mm, v(-27.24, 28.98) * mm, v(-28.3, 28.28) * mm, v(-29.52, 27.94) * mm, v(-30.3, 27.81) * mm], "startDerivative": vector(8.98, -0.37) * mm, "endDerivative": vector(-7.05, -1.02) * mm});
            skLineSegment(sketch, "E118", {"start": v(-20.99, 35.3) * mm, "end": v(-17.01, 35.3) * mm});
            skFitSpline(sketch, "E119", {"points": [v(-17.01, 35.3) * mm, v(-16.71, 34.98) * mm, v(-16.44, 34.33) * mm], "startDerivative": vector(0.72, -0.64) * mm, "endDerivative": vector(0.44, -1.3) * mm});
            skLineSegment(sketch, "E120", {"start": v(-16.44, 34.33) * mm, "end": v(-16.44, 21.93) * mm});
            skFitSpline(sketch, "E121", {"points": [v(-16.44, 21.93) * mm, v(-16.29, 21.48) * mm, v(-16.06, 21.15) * mm, v(-15.78, 20.92) * mm], "startDerivative": vector(0.36, -1.31) * mm, "endDerivative": vector(0.92, -0.67) * mm});
            skLineSegment(sketch, "E122", {"start": v(-15.78, 20.92) * mm, "end": v(-19.8, 20.92) * mm});
            skFitSpline(sketch, "E123", {"points": [v(-19.8, 20.92) * mm, v(-20.08, 21.15) * mm, v(-20.3, 21.63) * mm, v(-20.4, 21.93) * mm], "startDerivative": vector(-0.93, 0.57) * mm, "endDerivative": vector(-0.3, 0.92) * mm});
            skLineSegment(sketch, "E124", {"start": v(-20.4, 21.93) * mm, "end": v(-20.3, 34.09) * mm});
            skFitSpline(sketch, "E125", {"points": [v(-20.3, 34.09) * mm, v(-20.69, 34.9) * mm, v(-20.99, 35.3) * mm], "startDerivative": vector(-0.65, 1.57) * mm, "endDerivative": vector(-0.72, 0.83) * mm});
            skLineSegment(sketch, "E126", {"start": v(-14.16, 35.34) * mm, "end": v(-10.24, 35.34) * mm});
            skFitSpline(sketch, "E127", {"points": [v(-10.24, 35.34) * mm, v(-9.8, 35.07) * mm, v(-9.57, 34.66) * mm, v(-9.5, 34.34) * mm], "startDerivative": vector(1.36, -0.6) * mm, "endDerivative": vector(0.2, -1.08) * mm});
            skLineSegment(sketch, "E128", {"start": v(-9.5, 34.34) * mm, "end": v(-9.5, 25.13) * mm});
            skFitSpline(sketch, "E129", {"points": [v(-9.5, 25.13) * mm, v(-9.3, 24.5) * mm, v(-8.88, 23.84) * mm, v(-7.92, 23.36) * mm, v(-6.39, 23.36) * mm, v(-5.02, 24.52) * mm, v(-4.6, 25.78) * mm], "startDerivative": vector(1.25, -5) * mm, "endDerivative": vector(1.46, 7.1) * mm});
            skLineSegment(sketch, "E130", {"start": v(-4.6, 25.78) * mm, "end": v(-4.6, 33.9) * mm});
            skFitSpline(sketch, "E131", {"points": [v(-4.6, 33.9) * mm, v(-4.73, 34.45) * mm, v(-4.97, 35.03) * mm, v(-5.33, 35.34) * mm], "startDerivative": vector(-0.37, 1.58) * mm, "endDerivative": vector(-1.27, 0.86) * mm});
            skLineSegment(sketch, "E132", {"start": v(-5.33, 35.34) * mm, "end": v(-0.6, 35.34) * mm});
            skLineSegment(sketch, "E133", {"start": v(-0.6, 35.34) * mm, "end": v(-0.6, 22.2) * mm});
            skFitSpline(sketch, "E134", {"points": [v(-0.6, 22.2) * mm, v(-0.4, 21.58) * mm, v(-0.02, 20.95) * mm], "startDerivative": vector(0.36, -1.3) * mm, "endDerivative": vector(0.8, -1.2) * mm});
            skLineSegment(sketch, "E135", {"start": v(-0.02, 20.95) * mm, "end": v(-3.68, 20.95) * mm});
            skFitSpline(sketch, "E136", {"points": [v(-3.68, 20.95) * mm, v(-4.06, 21.2) * mm, v(-4.36, 21.6) * mm, v(-4.48, 21.86) * mm], "startDerivative": vector(-1.34, 0.4) * mm, "endDerivative": vector(-0.42, 0.83) * mm});
            skFitSpline(sketch, "E137", {"points": [v(-4.48, 21.86) * mm, v(-5.2, 21.22) * mm, v(-7.44, 20.47) * mm, v(-9.45, 20.5) * mm, v(-10.92, 20.9) * mm, v(-12.1, 21.65) * mm, v(-12.83, 22.55) * mm, v(-13.22, 23.39) * mm, v(-13.35, 23.93) * mm], "startDerivative": vector(-5.27, -6.07) * mm, "endDerivative": vector(-1.28, 6.28) * mm});
            skLineSegment(sketch, "E138", {"start": v(-13.35, 23.93) * mm, "end": v(-13.35, 34.07) * mm});
            skFitSpline(sketch, "E139", {"points": [v(-13.35, 34.07) * mm, v(-13.52, 34.58) * mm, v(-13.79, 34.99) * mm, v(-14.16, 35.34) * mm], "startDerivative": vector(-0.4, 1.54) * mm, "endDerivative": vector(-1.16, 1.01) * mm});
            skFitSpline(sketch, "E140", {"points": [v(1.67, 20.94) * mm, v(2.08, 21.33) * mm, v(2.36, 22.18) * mm], "startDerivative": vector(1.02, 0.74) * mm, "endDerivative": vector(0.4, 1.7) * mm});
            skLineSegment(sketch, "E141", {"start": v(2.36, 22.18) * mm, "end": v(2.36, 34.01) * mm});
            skFitSpline(sketch, "E142", {"points": [v(2.36, 34.01) * mm, v(2.23, 34.56) * mm, v(1.96, 35) * mm, v(1.66, 35.32) * mm], "startDerivative": vector(-0.3, 1.6) * mm, "endDerivative": vector(-1.01, 0.96) * mm});
            skLineSegment(sketch, "E143", {"start": v(1.66, 35.32) * mm, "end": v(7.02, 35.32) * mm});
            skFitSpline(sketch, "E144", {"points": [v(7.02, 35.32) * mm, v(7.45, 35.13) * mm, v(7.87, 34.64) * mm], "startDerivative": vector(0.96, -0.3) * mm, "endDerivative": vector(0.74, -1.05) * mm});
            skLineSegment(sketch, "E145", {"start": v(7.87, 34.64) * mm, "end": v(10.66, 28.46) * mm});
            skLineSegment(sketch, "E146", {"start": v(10.66, 28.46) * mm, "end": v(13.24, 34.64) * mm});
            skFitSpline(sketch, "E147", {"points": [v(13.24, 34.64) * mm, v(13.54, 35.03) * mm, v(13.97, 35.3) * mm, v(14.2, 35.32) * mm], "startDerivative": vector(0.71, 1.1) * mm, "endDerivative": vector(0.8, 0) * mm});
            skLineSegment(sketch, "E148", {"start": v(14.2, 35.32) * mm, "end": v(19.09, 35.32) * mm});
            skFitSpline(sketch, "E149", {"points": [v(19.09, 35.32) * mm, v(18.86, 35.17) * mm, v(18.6, 34.72) * mm, v(18.4, 34.05) * mm], "startDerivative": vector(-0.91, -0.46) * mm, "endDerivative": vector(-0.4, -1.72) * mm});
            skLineSegment(sketch, "E150", {"start": v(18.4, 34.05) * mm, "end": v(18.4, 21.94) * mm});
            skFitSpline(sketch, "E151", {"points": [v(18.4, 21.94) * mm, v(18.61, 21.44) * mm, v(19.19, 20.88) * mm], "startDerivative": vector(0.34, -1.13) * mm, "endDerivative": vector(1.22, -0.98) * mm});
            skLineSegment(sketch, "E152", {"start": v(19.19, 20.88) * mm, "end": v(14.41, 20.88) * mm});
            skFitSpline(sketch, "E153", {"points": [v(14.41, 20.88) * mm, v(14.71, 21.36) * mm, v(14.92, 22.02) * mm, v(15.02, 22.54) * mm, v(15.04, 22.52) * mm], "startDerivative": vector(1.09, 1.54) * mm, "endDerivative": vector(0.34, -0.57) * mm});
            skLineSegment(sketch, "E154", {"start": v(15.04, 22.52) * mm, "end": v(15.04, 31.22) * mm});
            skLineSegment(sketch, "E155", {"start": v(15.04, 31.22) * mm, "end": v(14.61, 30.44) * mm});
            skLineSegment(sketch, "E156", {"start": v(14.61, 30.44) * mm, "end": v(13.5, 28.15) * mm});
            skLineSegment(sketch, "E157", {"start": v(13.5, 28.15) * mm, "end": v(12.2, 24.78) * mm});
            skFitSpline(sketch, "E158", {"points": [v(12.2, 24.78) * mm, v(11.95, 24.43) * mm, v(11.65, 24.13) * mm, v(11.3, 24.08) * mm, v(10.74, 24.05) * mm, v(10.09, 24.05) * mm, v(9.56, 24.15) * mm, v(8.88, 24.78) * mm, v(8.28, 25.48) * mm], "startDerivative": vector(-2.37, -3.57) * mm, "endDerivative": vector(-5.03, 3.6) * mm});
            skFitSpline(sketch, "E159", {"points": [v(8.28, 25.48) * mm, v(6.95, 27.62) * mm, v(5.46, 30.51) * mm], "startDerivative": vector(-2.86, 4.36) * mm, "endDerivative": vector(-2.77, 5.67) * mm});
            skLineSegment(sketch, "E160", {"start": v(5.46, 30.51) * mm, "end": v(5.46, 22.08) * mm});
            skFitSpline(sketch, "E161", {"points": [v(5.46, 22.08) * mm, v(5.56, 21.6) * mm, v(6.13, 20.91) * mm], "startDerivative": vector(0.07, -1.1) * mm, "endDerivative": vector(1.2, -1.22) * mm});
            skLineSegment(sketch, "E162", {"start": v(6.13, 20.91) * mm, "end": v(1.67, 20.94) * mm});
            skLineSegment(sketch, "E163", {"start": v(20.84, 35.38) * mm, "end": v(29.3, 35.53) * mm});
            skFitSpline(sketch, "E164", {"points": [v(29.3, 35.53) * mm, v(30.85, 34.87) * mm, v(32.4, 32.78) * mm, v(32.8, 30.9) * mm, v(32.44, 29.04) * mm, v(31.1, 27.46) * mm, v(29, 26.26) * mm, v(25.6, 25.3) * mm], "startDerivative": vector(12.8, -3.36) * mm, "endDerivative": vector(-20.32, -4.78) * mm});
            skFitSpline(sketch, "E165", {"points": [v(25.56, 27.82) * mm, v(26.7, 28.09) * mm, v(28.16, 28.74) * mm, v(29.09, 30.03) * mm, v(29.24, 31.52) * mm, v(28.4, 32.6) * mm, v(26.46, 32.84) * mm, v(25.6, 32.78) * mm], "startDerivative": vector(8.38, 1.76) * mm, "endDerivative": vector(-6.65, -0.61) * mm});
            skLineSegment(sketch, "E166", {"start": v(25.6, 32.78) * mm, "end": v(25.56, 27.82) * mm});
            skLineSegment(sketch, "E167", {"start": v(25.6, 25.3) * mm, "end": v(25.6, 21.84) * mm});
            skFitSpline(sketch, "E168", {"points": [v(25.6, 21.84) * mm, v(25.38, 21.39) * mm, v(24.6, 20.94) * mm], "startDerivative": vector(-0.3, -1.1) * mm, "endDerivative": vector(-1.6, -0.7) * mm});
            skLineSegment(sketch, "E169", {"start": v(24.6, 20.94) * mm, "end": v(20.75, 20.94) * mm});
            skFitSpline(sketch, "E170", {"points": [v(20.75, 20.94) * mm, v(21.14, 21.48) * mm, v(21.47, 22.38) * mm, v(21.47, 23.1) * mm], "startDerivative": vector(1.3, 1.56) * mm, "endDerivative": vector(-0.2, 2.14) * mm});
            skLineSegment(sketch, "E171", {"start": v(21.47, 23.1) * mm, "end": v(21.47, 34.24) * mm});
            skFitSpline(sketch, "E172", {"points": [v(21.47, 34.24) * mm, v(21.32, 34.63) * mm, v(20.9, 35.14) * mm, v(20.84, 35.38) * mm], "startDerivative": vector(-0.26, 1.14) * mm, "endDerivative": vector(-0.04, 0.88) * mm});
            skLineSegment(sketch, "E173", {"start": v(-25.52, 34.9) * mm, "end": v(-26.79, 35.23) * mm});
            skSolve(sketch);
        }
        {
            var Q0;
            {var subQ5=sQuery(id+"F12.wireOp",EDGE,"E60");Q0=makeQuery(id+"F12.imprint","IMPRINT",FACE,{"disambiguationData":[TD([[makeQuery(id+"F12.imprint","IMPRINT",EDGE,{"derivedFrom":subQ5}),-1.0]])]});}
            var Q1;
            Q1=makeQuery(id+"F12.imprint","IMPRINT",FACE,{"disambiguationData":[TD([[makeQuery(id+"F12.imprint","IMPRINT",EDGE,{"derivedFrom":sQuery(id+"F12.wireOp",EDGE,"E118")}),-1.0]])]});
            var Q2;
            Q2=makeQuery(id+"F12.imprint","IMPRINT",FACE,{"disambiguationData":[TD([[makeQuery(id+"F12.imprint","IMPRINT",EDGE,{"derivedFrom":sQuery(id+"F12.wireOp",EDGE,"E126")}),-1.0]])]});
            var Q3;
            Q3=makeQuery(id+"F12.imprint","IMPRINT",FACE,{"disambiguationData":[TD([[makeQuery(id+"F12.imprint","IMPRINT",EDGE,{"derivedFrom":sQuery(id+"F12.wireOp",EDGE,"E140")}),-1.0]])]});
            var Q4;
            Q4=makeQuery(id+"F12.imprint","IMPRINT",FACE,{"disambiguationData":[TD([[makeQuery(id+"F12.imprint","IMPRINT",EDGE,{"derivedFrom":sQuery(id+"F12.wireOp",EDGE,"E163")}),-1.0]])]});
            var Q5;
            {var subQ0=sQuery(id+"F12.wireOp",EDGE,"E62");var subQ1=sQuery(id+"F12.wireOp",EDGE,"E61");var subQ2=makeQuery(id+"F12.imprint","INTERSECT",VERTEX,{"derivedFrom":[subQ1,subQ0]});Q5=makeQuery(id+"F12.imprint","IMPRINT",FACE,{"disambiguationData":[TD([[makeQuery(id+"F12.imprint","IMPRINT",EDGE,{"disambiguationData":[TD([[subQ2,1.0]])],"derivedFrom":subQ1}),-1.0]])]});}
            var Q6;
            Q6=makeQuery(id+"F12.imprint","IMPRINT",FACE,{"disambiguationData":[TD([[makeQuery(id+"F12.imprint","IMPRINT",EDGE,{"derivedFrom":sQuery(id+"F12.wireOp",EDGE,"E84")}),-1.0]])]});
            extrude(context, id + "F13", {"entities" : qUnion([Q0, Q1, Q2, Q3, Q4, Q5, Q6]), "operationType" : NewBodyOperationType.REMOVE, "oppositeDirection" : true, "depth" : 1 * mm, "offsetDistance" : 25 * mm});
        }
        {
            var Q0;
            Q0=qCreatedBy(makeId("Right.planeOp"),FACE);
            var sketch = newSketch(context, id + "F14", { "sketchPlane" : qUnion([Q0])});
            skLineSegment(sketch, "E174.bottom", {"start": v(-85.88, 30) * mm, "end": v(-75.88, 30) * mm});
            skLineSegment(sketch, "E174.top", {"start": v(-85.88, 47) * mm, "end": v(-75.88, 47) * mm});
            skLineSegment(sketch, "E174.left", {"start": v(-85.88, 30) * mm, "end": v(-85.88, 47) * mm});
            skLineSegment(sketch, "E174.right", {"start": v(-75.88, 30) * mm, "end": v(-75.88, 47) * mm});
            skLineSegment(sketch, "E175.bottom", {"start": v(-75.88, 47) * mm, "end": v(-63.88, 47) * mm});
            skLineSegment(sketch, "E175.top", {"start": v(-75.88, 40) * mm, "end": v(-63.88, 40) * mm});
            skLineSegment(sketch, "E175.left", {"start": v(-75.88, 47) * mm, "end": v(-75.88, 40) * mm});
            skLineSegment(sketch, "E175.right", {"start": v(-63.88, 47) * mm, "end": v(-63.88, 40) * mm});
            skLineSegment(sketch, "E176", {"start": v(-75.88, 30) * mm, "end": v(-63.88, 40) * mm});
            skLineSegment(sketch, "E177", {"start": v(-63.88, 40) * mm, "end": v(-63.88, 30) * mm});
            skLineSegment(sketch, "E178", {"start": v(-63.88, 30) * mm, "end": v(-75.88, 30) * mm});
            skSolve(sketch);
        }
        {
            var Q0;
            Q0=makeQuery(id+"F14.imprint","IMPRINT",FACE,{"disambiguationData":[TD([[makeQuery(id+"F14.imprint","IMPRINT",EDGE,{"derivedFrom":sQuery(id+"F14.wireOp",EDGE,"E174.bottom")}),1.0]])]});
            var Q1;
            Q1=makeQuery(id+"F14.imprint","IMPRINT",FACE,{"disambiguationData":[TD([[makeQuery(id+"F14.imprint","IMPRINT",EDGE,{"derivedFrom":sQuery(id+"F14.wireOp",EDGE,"E175.bottom")}),-1.0]])]});
            extrude(context, id + "F15", {"entities" : qUnion([Q0, Q1]), "operationType" : NewBodyOperationType.ADD, "endBound" : BoundingType.SYMMETRIC, "depth" : 150 * mm, "offsetDistance" : 25 * mm});
        }
        {
            var Q0;
            Q0=makeQuery(id+"F14.imprint","IMPRINT",FACE,{"disambiguationData":[TD([[makeQuery(id+"F14.imprint","IMPRINT",EDGE,{"derivedFrom":sQuery(id+"F14.wireOp",EDGE,"E174.right")}),-1.0]])]});
            var Q1;
            Q1=makeQuery(id+"F14.imprint","IMPRINT",FACE,{"disambiguationData":[TD([[makeQuery(id+"F14.imprint","IMPRINT",EDGE,{"derivedFrom":sQuery(id+"F14.wireOp",EDGE,"E176")}),-1.0]])]});
            extrude(context, id + "F16", {"entities" : qUnion([Q0, Q1]), "operationType" : NewBodyOperationType.ADD, "endBound" : BoundingType.SYMMETRIC, "depth" : 25 * mm, "offsetDistance" : 25 * mm});
        }
        {
            var Q0;
            Q0=makeQuery(id+"F15.opExtrude","CAP_FACE",FACE,{"disambiguationData":[OSD([sQuery(id+"F14.wireOp",EDGE,"E174.bottom"),sQuery(id+"F14.wireOp",EDGE,"E174.top"),sQuery(id+"F14.wireOp",EDGE,"E174.left"),sQuery(id+"F14.wireOp",EDGE,"E174.right"),sQuery(id+"F14.wireOp",EDGE,"E175.bottom"),sQuery(id+"F14.wireOp",EDGE,"E175.top"),sQuery(id+"F14.wireOp",EDGE,"E175.right")])],"isStart":true});
            var sketch = newSketch(context, id + "F17", { "sketchPlane" : qUnion([Q0])});
            skLineSegment(sketch, "E179.bottom", {"start": v(63.88, 40) * mm, "end": v(75.88, 40) * mm});
            skLineSegment(sketch, "E179.top", {"start": v(63.88, 30) * mm, "end": v(75.88, 30) * mm});
            skLineSegment(sketch, "E179.left", {"start": v(63.88, 40) * mm, "end": v(63.88, 30) * mm});
            skLineSegment(sketch, "E179.right", {"start": v(75.88, 40) * mm, "end": v(75.88, 30) * mm});
            skSolve(sketch);
        }
        {
            var Q0;
            Q0=makeQuery(id+"F17.imprint","IMPRINT",FACE,{"disambiguationData":[TD([[makeQuery(id+"F17.imprint","IMPRINT",EDGE,{"derivedFrom":sQuery(id+"F17.wireOp",EDGE,"E179.bottom")}),1.0]])]});
            extrude(context, id + "F18", {"entities" : qUnion([Q0]), "operationType" : NewBodyOperationType.ADD, "oppositeDirection" : true, "depth" : 15 * mm, "offsetDistance" : 25 * mm});
        }
        {
            var Q0;
            Q0=makeQuery(id+"F15.opExtrude","CAP_FACE",FACE,{"disambiguationData":[OSD([sQuery(id+"F14.wireOp",EDGE,"E174.bottom"),sQuery(id+"F14.wireOp",EDGE,"E174.top"),sQuery(id+"F14.wireOp",EDGE,"E174.left"),sQuery(id+"F14.wireOp",EDGE,"E174.right"),sQuery(id+"F14.wireOp",EDGE,"E175.bottom"),sQuery(id+"F14.wireOp",EDGE,"E175.top"),sQuery(id+"F14.wireOp",EDGE,"E175.right")])],"isStart":false});
            var sketch = newSketch(context, id + "F19", { "sketchPlane" : qUnion([Q0])});
            skLineSegment(sketch, "E180.bottom", {"start": v(-75.88, 40) * mm, "end": v(-63.88, 40) * mm});
            skLineSegment(sketch, "E180.top", {"start": v(-75.88, 30) * mm, "end": v(-63.88, 30) * mm});
            skLineSegment(sketch, "E180.left", {"start": v(-75.88, 40) * mm, "end": v(-75.88, 30) * mm});
            skLineSegment(sketch, "E180.right", {"start": v(-63.88, 40) * mm, "end": v(-63.88, 30) * mm});
            skSolve(sketch);
        }
        {
            var Q0;
            Q0=makeQuery(id+"F19.imprint","IMPRINT",FACE,{"disambiguationData":[TD([[makeQuery(id+"F19.imprint","IMPRINT",EDGE,{"derivedFrom":sQuery(id+"F19.wireOp",EDGE,"E180.bottom")}),-1.0]])]});
            extrude(context, id + "F20", {"entities" : qUnion([Q0]), "operationType" : NewBodyOperationType.ADD, "oppositeDirection" : true, "depth" : 15 * mm, "offsetDistance" : 25 * mm});
        }
        {
            var Q0;
            Q0=makeQuery(id+"F15.opExtrude","SWEPT_EDGE",EDGE,{"disambiguationData":[OSD([sQuery(id+"F14.wireOp",EDGE,"E174.top"),sQuery(id+"F14.wireOp",EDGE,"E174.left")])]});
            var Q1;
            Q1=makeQuery(id+"F15.opExtrude","CAP_EDGE",EDGE,{"disambiguationData":[OSD([sQuery(id+"F14.wireOp",EDGE,"E174.left")])],"isStart":false});
            var Q2;
            Q2=makeQuery(id+"F15.opExtrude","CAP_EDGE",EDGE,{"disambiguationData":[OSD([sQuery(id+"F14.wireOp",EDGE,"E174.top"),sQuery(id+"F14.wireOp",EDGE,"E175.bottom")])],"isStart":false});
            var Q3;
            Q3=makeQuery(id+"F15.opExtrude","CAP_EDGE",EDGE,{"disambiguationData":[OSD([sQuery(id+"F14.wireOp",EDGE,"E174.left")])],"isStart":true});
            var Q4;
            Q4=makeQuery(id+"F15.opExtrude","CAP_EDGE",EDGE,{"disambiguationData":[OSD([sQuery(id+"F14.wireOp",EDGE,"E174.top"),sQuery(id+"F14.wireOp",EDGE,"E175.bottom")])],"isStart":true});
            fillet(context, id + "F21", {"entities" : qUnion([Q0, Q1, Q2, Q3, Q4]), "radius" : 8 * mm, "tangentPropagation" : true, "allowEdgeOverflow" : false});
        }
    });
